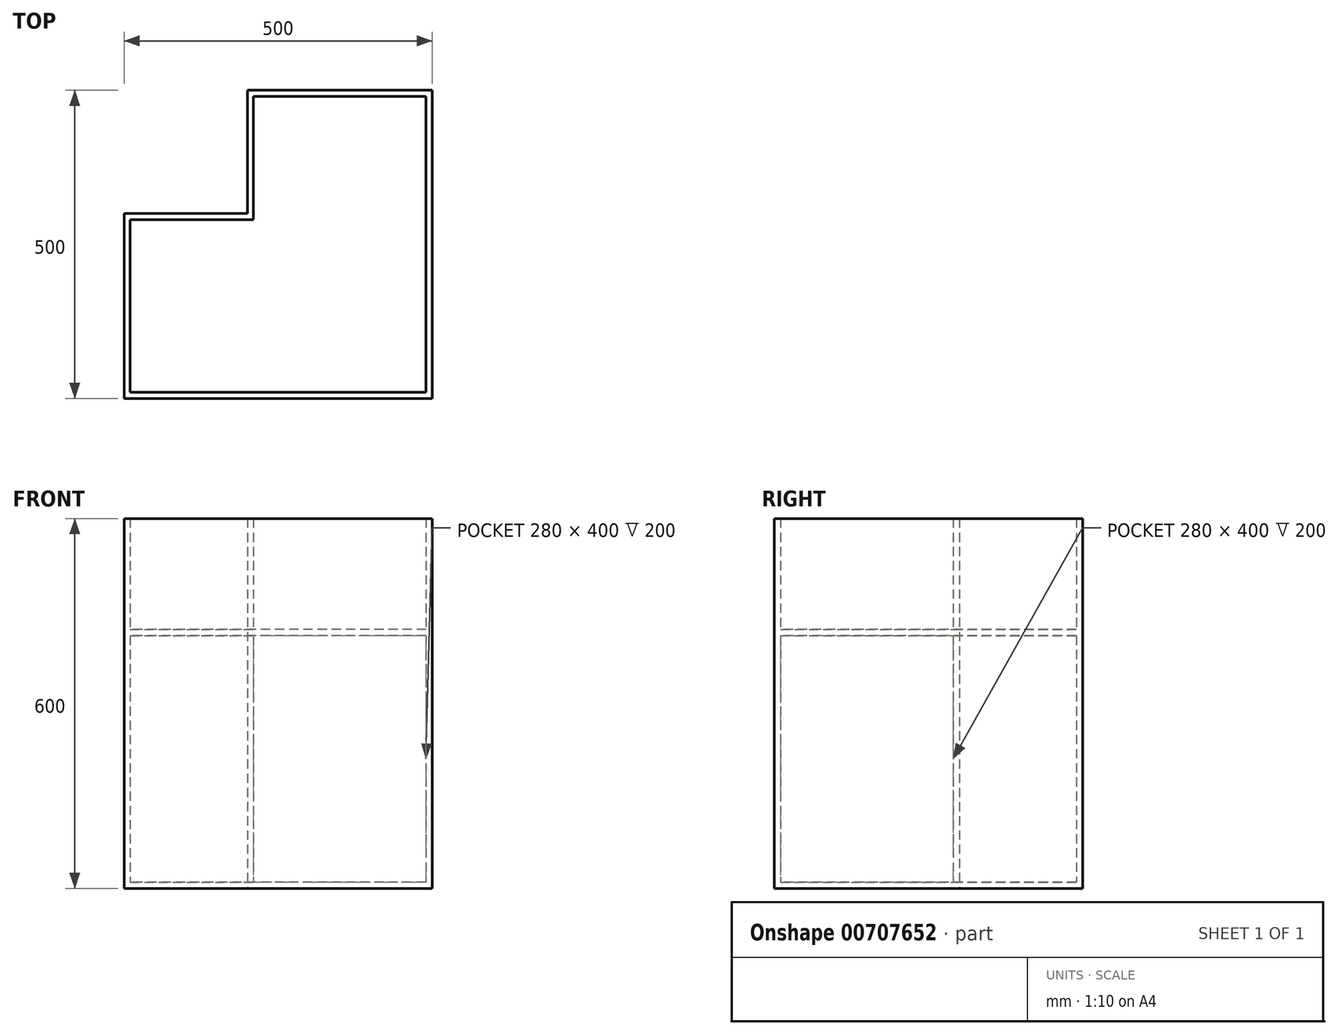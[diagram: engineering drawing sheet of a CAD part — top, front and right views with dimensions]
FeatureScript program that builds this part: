
annotation { "Feature Type Name" : "Feature", "Feature Type Description" : "" }
export const myFeature = defineFeature(function(context is Context, id is Id, definition is map)
    precondition{}
    {
        {
            var Q0;
            Q0=qCreatedBy(makeId("Top.planeOp"),FACE);
            var sketch = newSketch(context, id + "F0", { "sketchPlane" : qUnion([Q0])});
            skLineSegment(sketch, "E0.top", {"start": v(250, -250) * mm, "end": v(-250, -250) * mm});
            skLineSegment(sketch, "E0.left", {"start": v(250, 250) * mm, "end": v(250, -250) * mm});
            skPoint(sketch, "E0.middle", {"position": v(0, 0) * mm});
            skLineSegment(sketch, "E1", {"start": v(250, 250) * mm, "end": v(-50, 250) * mm});
            skLineSegment(sketch, "E2", {"start": v(-250, -250) * mm, "end": v(-250, 50) * mm});
            skLineSegment(sketch, "E3", {"start": v(-250, 50) * mm, "end": v(-50, 50) * mm});
            skLineSegment(sketch, "E4", {"start": v(-50, 50) * mm, "end": v(-50, 250) * mm});
            skSolve(sketch);
        }
        {
            var Q0;
            Q0=makeQuery(id+"F0.imprint","IMPRINT",FACE,{"disambiguationData":[TD([[makeQuery(id+"F0.imprint","IMPRINT",EDGE,{"derivedFrom":sQuery(id+"F0.wireOp",EDGE,"E0.bottom")}),1.0]])]});
            var Q1;
            Q1=makeQuery(id+"F0.imprint","IMPRINT",FACE,{"disambiguationData":[TD([[makeQuery(id+"F0.imprint","IMPRINT",EDGE,{"derivedFrom":sQuery(id+"F0.wireOp",EDGE,"E0.top")}),-1.0]])]});
            extrude(context, id + "F1", {"entities" : qUnion([Q0, Q1]), "depth" : 600 * mm, "offsetDistance" : 25 * mm});
        }
        {
            var Q0;
            Q0=makeQuery(id+"F1.opExtrude","CAP_FACE",FACE,{"disambiguationData":[OSD([sQuery(id+"F0.wireOp",EDGE,"E0.bottom"),sQuery(id+"F0.wireOp",EDGE,"E0.top"),sQuery(id+"F0.wireOp",EDGE,"E0.left"),sQuery(id+"F0.wireOp",EDGE,"E0.right")])],"isStart":false});
            shell(context, id + "F2", {"entities" : qUnion([Q0]), "thickness" : 10 * mm});
        }
        {
            var Q0;
            Q0=makeQuery(id+"F2.opShell","OFFSET_FACE",FACE,{"disambiguationData":[OSD([sQuery(id+"F0.wireOp",EDGE,"E0.top"),sQuery(id+"F0.wireOp",EDGE,"E0.left"),sQuery(id+"F0.wireOp",EDGE,"E1"),sQuery(id+"F0.wireOp",EDGE,"E2"),sQuery(id+"F0.wireOp",EDGE,"E3"),sQuery(id+"F0.wireOp",EDGE,"E4")])]});
            cPlane(context, id + "F3", {"entities" : qUnion([Q0]), "cplaneType" : CPlaneType.OFFSET, "offset" : 400 * mm, "width" : 150 * mm, "height" : 150 * mm});
        }
        {
            var Q0;
            Q0=qCreatedBy(id+"F3.planeOp",FACE);
            var sketch = newSketch(context, id + "F4", { "sketchPlane" : qUnion([Q0])});
            skLineSegment(sketch, "E5.0", {"start": v(-240, -240) * mm, "end": v(-240, 40) * mm});
            skPoint(sketch, "E6.0", {"position": v(-140, 40) * mm});
            skLineSegment(sketch, "E7.0", {"start": v(-240, 40) * mm, "end": v(-40, 40) * mm});
            skLineSegment(sketch, "E8.0", {"start": v(-40, 40) * mm, "end": v(-40, 240) * mm});
            skLineSegment(sketch, "E9.0", {"start": v(240, 240) * mm, "end": v(-40, 240) * mm});
            skLineSegment(sketch, "E10.0", {"start": v(240, 240) * mm, "end": v(240, -240) * mm});
            skLineSegment(sketch, "E11.0", {"start": v(240, -240) * mm, "end": v(-240, -240) * mm});
            skSolve(sketch);
        }
        {
            var Q0;
            Q0=makeQuery(id+"F4.imprint","IMPRINT",FACE,{"disambiguationData":[TD([[makeQuery(id+"F4.imprint","IMPRINT",EDGE,{"derivedFrom":sQuery(id+"F4.wireOp",EDGE,"37c88102-f814-48c6-88fc-a3c0d9feb177.0")}),-1.0]])]});
            var Q1;
            Q1=makeQuery(id+"F4.imprint","IMPRINT",FACE,{"disambiguationData":[TD([[makeQuery(id+"F4.imprint","IMPRINT",EDGE,{"derivedFrom":sQuery(id+"F4.wireOp",EDGE,"E5.0")}),-1.0]])]});
            extrude(context, id + "F5", {"entities" : qUnion([Q0, Q1]), "operationType" : NewBodyOperationType.ADD, "depth" : 10 * mm, "offsetDistance" : 25 * mm});
        }
    });
